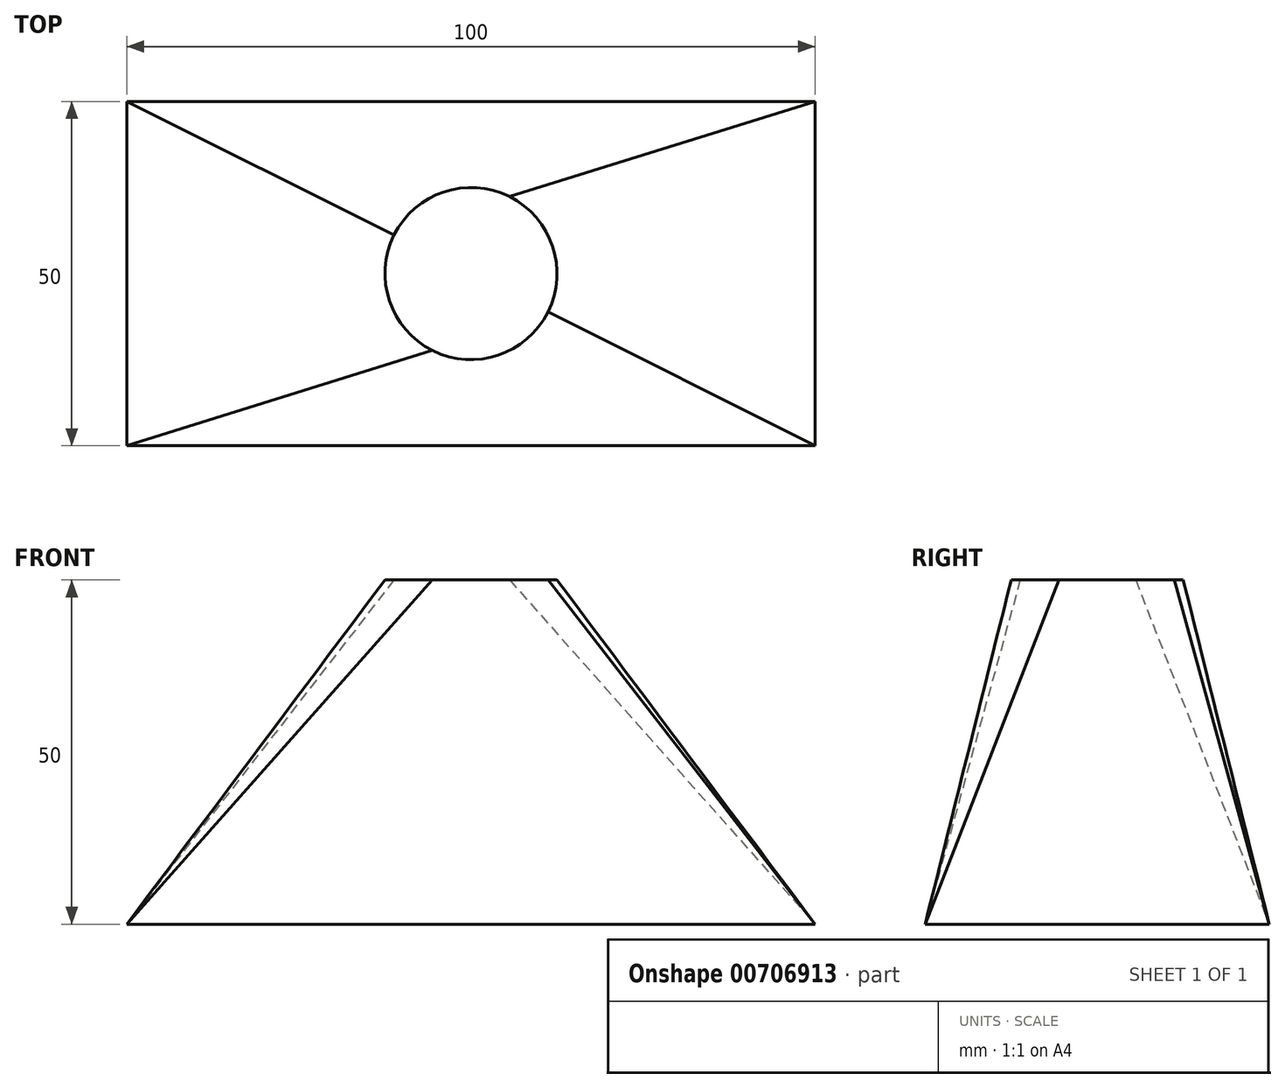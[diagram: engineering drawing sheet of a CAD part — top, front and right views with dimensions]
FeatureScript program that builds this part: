
annotation { "Feature Type Name" : "Feature", "Feature Type Description" : "" }
export const myFeature = defineFeature(function(context is Context, id is Id, definition is map)
    precondition{}
    {
        {
            var Q0;
            Q0=qCreatedBy(makeId("Top.planeOp"),FACE);
            var sketch = newSketch(context, id + "F0", { "sketchPlane" : qUnion([Q0])});
            skLineSegment(sketch, "E0.bottom", {"start": v(-50, 25) * mm, "end": v(50, 25) * mm});
            skLineSegment(sketch, "E0.top", {"start": v(-50, -25) * mm, "end": v(50, -25) * mm});
            skLineSegment(sketch, "E0.left", {"start": v(-50, 25) * mm, "end": v(-50, -25) * mm});
            skLineSegment(sketch, "E0.right", {"start": v(50, 25) * mm, "end": v(50, -25) * mm});
            skSolve(sketch);
        }
        {
            var Q0;
            Q0=qCreatedBy(makeId("Top.planeOp"),FACE);
            cPlane(context, id + "F1", {"entities" : qUnion([Q0]), "cplaneType" : CPlaneType.OFFSET, "offset" : 50 * mm, "width" : 150 * mm, "height" : 150 * mm});
        }
        {
            var Q0;
            Q0=qCreatedBy(id+"F1.planeOp",FACE);
            var sketch = newSketch(context, id + "F2", { "sketchPlane" : qUnion([Q0])});
            skCircle(sketch, "E1", {"center": v(0, 0) * mm, "radius": 12.5 * mm});
            skSolve(sketch);
        }
        {
            var Q0;
            Q0=makeQuery(id+"F2.imprint","IMPRINT",FACE,{"disambiguationData":[TD([[makeQuery(id+"F2.imprint","IMPRINT",EDGE,{"derivedFrom":sQuery(id+"F2.wireOp",EDGE,"E1")}),1.0]])]});
            var Q1;
            Q1=makeQuery(id+"F0.imprint","IMPRINT",FACE,{"disambiguationData":[TD([[makeQuery(id+"F0.imprint","IMPRINT",EDGE,{"derivedFrom":sQuery(id+"F0.wireOp",EDGE,"E0.bottom")}),-1.0]])]});
            loft(context, id + "F3", {"sheetProfilesArray" : [{ "sheetProfileEntities" : qUnion([Q0]) }, { "sheetProfileEntities" : qUnion([Q1]) }]});
        }
    });
